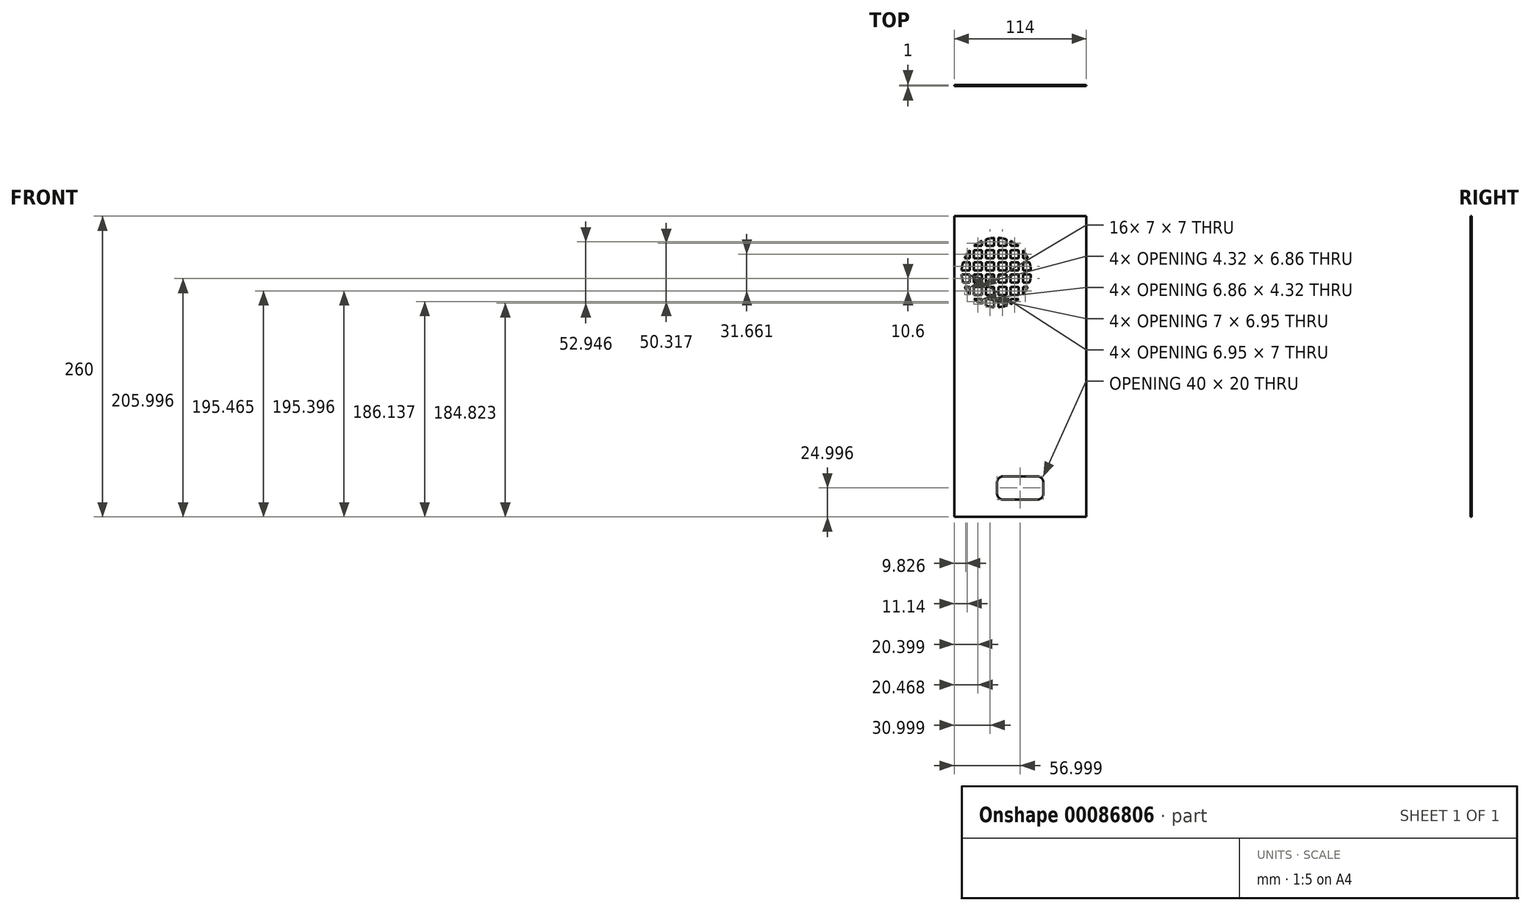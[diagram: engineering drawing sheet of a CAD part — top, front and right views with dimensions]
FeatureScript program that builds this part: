
annotation { "Feature Type Name" : "Feature", "Feature Type Description" : "" }
export const myFeature = defineFeature(function(context is Context, id is Id, definition is map)
    precondition{}
    {
        {
            var Q0;
            Q0=qCreatedBy(makeId("Front.planeOp"),FACE);
            var sketch = newSketch(context, id + "F0", { "sketchPlane" : qUnion([Q0])});
            skLineSegment(sketch, "E0.bottom", {"start": v(-87.72, 200.1) * mm, "end": v(26.28, 200.1) * mm});
            skLineSegment(sketch, "E0.top", {"start": v(-87.72, -59.9) * mm, "end": v(26.28, -59.9) * mm});
            skLineSegment(sketch, "E0.left", {"start": v(-87.72, 200.1) * mm, "end": v(-87.72, -59.9) * mm});
            skLineSegment(sketch, "E0.right", {"start": v(26.28, 200.1) * mm, "end": v(26.28, -59.9) * mm});
            skCircle(sketch, "E1", {"center": v(-51.42, 151.4) * mm, "radius": 30 * mm});
            skLineSegment(sketch, "E2.bottom", {"start": v(-81.42, 181.4) * mm, "end": v(-74.42, 181.4) * mm});
            skLineSegment(sketch, "E2.top", {"start": v(-81.42, 174.4) * mm, "end": v(-74.42, 174.4) * mm});
            skLineSegment(sketch, "E2.left", {"start": v(-81.42, 181.4) * mm, "end": v(-81.42, 174.4) * mm});
            skLineSegment(sketch, "E2.right", {"start": v(-74.42, 181.4) * mm, "end": v(-74.42, 174.4) * mm});
            skLineSegment(sketch, "E3.0.1.0", {"start": v(-81.42, 163.8) * mm, "end": v(-74.42, 163.8) * mm});
            skLineSegment(sketch, "E3.0.1.1", {"start": v(-81.42, 170.8) * mm, "end": v(-81.42, 163.8) * mm});
            skLineSegment(sketch, "E3.0.1.2", {"start": v(-74.42, 170.8) * mm, "end": v(-74.42, 163.8) * mm});
            skLineSegment(sketch, "E3.0.1.3", {"start": v(-81.42, 170.8) * mm, "end": v(-74.42, 170.8) * mm});
            skLineSegment(sketch, "E3.0.2.0", {"start": v(-81.42, 153.2) * mm, "end": v(-74.42, 153.2) * mm});
            skLineSegment(sketch, "E3.0.2.1", {"start": v(-81.42, 160.2) * mm, "end": v(-81.42, 153.2) * mm});
            skLineSegment(sketch, "E3.0.2.2", {"start": v(-74.42, 160.2) * mm, "end": v(-74.42, 153.2) * mm});
            skLineSegment(sketch, "E3.0.2.3", {"start": v(-81.42, 160.2) * mm, "end": v(-74.42, 160.2) * mm});
            skLineSegment(sketch, "E3.0.3.0", {"start": v(-81.42, 142.6) * mm, "end": v(-74.42, 142.6) * mm});
            skLineSegment(sketch, "E3.0.3.1", {"start": v(-81.42, 149.6) * mm, "end": v(-81.42, 142.6) * mm});
            skLineSegment(sketch, "E3.0.3.2", {"start": v(-74.42, 149.6) * mm, "end": v(-74.42, 142.6) * mm});
            skLineSegment(sketch, "E3.0.3.3", {"start": v(-81.42, 149.6) * mm, "end": v(-74.42, 149.6) * mm});
            skLineSegment(sketch, "E3.0.4.0", {"start": v(-81.42, 132) * mm, "end": v(-74.42, 132) * mm});
            skLineSegment(sketch, "E3.0.4.1", {"start": v(-81.42, 139) * mm, "end": v(-81.42, 132) * mm});
            skLineSegment(sketch, "E3.0.4.2", {"start": v(-74.42, 139) * mm, "end": v(-74.42, 132) * mm});
            skLineSegment(sketch, "E3.0.4.3", {"start": v(-81.42, 139) * mm, "end": v(-74.42, 139) * mm});
            skLineSegment(sketch, "E3.0.5.0", {"start": v(-81.42, 121.4) * mm, "end": v(-74.42, 121.4) * mm});
            skLineSegment(sketch, "E3.0.5.1", {"start": v(-81.42, 128.4) * mm, "end": v(-81.42, 121.4) * mm});
            skLineSegment(sketch, "E3.0.5.2", {"start": v(-74.42, 128.4) * mm, "end": v(-74.42, 121.4) * mm});
            skLineSegment(sketch, "E3.0.5.3", {"start": v(-81.42, 128.4) * mm, "end": v(-74.42, 128.4) * mm});
            skLineSegment(sketch, "E3.0.6.0", {"start": v(-81.42, 110.8) * mm, "end": v(-74.42, 110.8) * mm});
            skLineSegment(sketch, "E3.0.6.1", {"start": v(-81.42, 117.8) * mm, "end": v(-81.42, 110.8) * mm});
            skLineSegment(sketch, "E3.0.6.2", {"start": v(-74.42, 117.8) * mm, "end": v(-74.42, 110.8) * mm});
            skLineSegment(sketch, "E3.0.6.3", {"start": v(-81.42, 117.8) * mm, "end": v(-74.42, 117.8) * mm});
            skLineSegment(sketch, "E3.1.0.0", {"start": v(-70.82, 174.4) * mm, "end": v(-63.82, 174.4) * mm});
            skLineSegment(sketch, "E3.1.0.1", {"start": v(-70.82, 181.4) * mm, "end": v(-70.82, 174.4) * mm});
            skLineSegment(sketch, "E3.1.0.2", {"start": v(-63.82, 181.4) * mm, "end": v(-63.82, 174.4) * mm});
            skLineSegment(sketch, "E3.1.0.3", {"start": v(-70.82, 181.4) * mm, "end": v(-63.82, 181.4) * mm});
            skLineSegment(sketch, "E3.1.1.0", {"start": v(-70.82, 163.8) * mm, "end": v(-63.82, 163.8) * mm});
            skLineSegment(sketch, "E3.1.1.1", {"start": v(-70.82, 170.8) * mm, "end": v(-70.82, 163.8) * mm});
            skLineSegment(sketch, "E3.1.1.2", {"start": v(-63.82, 170.8) * mm, "end": v(-63.82, 163.8) * mm});
            skLineSegment(sketch, "E3.1.1.3", {"start": v(-70.82, 170.8) * mm, "end": v(-63.82, 170.8) * mm});
            skLineSegment(sketch, "E3.1.2.0", {"start": v(-70.82, 153.2) * mm, "end": v(-63.82, 153.2) * mm});
            skLineSegment(sketch, "E3.1.2.1", {"start": v(-70.82, 160.2) * mm, "end": v(-70.82, 153.2) * mm});
            skLineSegment(sketch, "E3.1.2.2", {"start": v(-63.82, 160.2) * mm, "end": v(-63.82, 153.2) * mm});
            skLineSegment(sketch, "E3.1.2.3", {"start": v(-70.82, 160.2) * mm, "end": v(-63.82, 160.2) * mm});
            skLineSegment(sketch, "E3.1.3.0", {"start": v(-70.82, 142.6) * mm, "end": v(-63.82, 142.6) * mm});
            skLineSegment(sketch, "E3.1.3.1", {"start": v(-70.82, 149.6) * mm, "end": v(-70.82, 142.6) * mm});
            skLineSegment(sketch, "E3.1.3.2", {"start": v(-63.82, 149.6) * mm, "end": v(-63.82, 142.6) * mm});
            skLineSegment(sketch, "E3.1.3.3", {"start": v(-70.82, 149.6) * mm, "end": v(-63.82, 149.6) * mm});
            skLineSegment(sketch, "E3.1.4.0", {"start": v(-70.82, 132) * mm, "end": v(-63.82, 132) * mm});
            skLineSegment(sketch, "E3.1.4.1", {"start": v(-70.82, 139) * mm, "end": v(-70.82, 132) * mm});
            skLineSegment(sketch, "E3.1.4.2", {"start": v(-63.82, 139) * mm, "end": v(-63.82, 132) * mm});
            skLineSegment(sketch, "E3.1.4.3", {"start": v(-70.82, 139) * mm, "end": v(-63.82, 139) * mm});
            skLineSegment(sketch, "E3.1.5.0", {"start": v(-70.82, 121.4) * mm, "end": v(-63.82, 121.4) * mm});
            skLineSegment(sketch, "E3.1.5.1", {"start": v(-70.82, 128.4) * mm, "end": v(-70.82, 121.4) * mm});
            skLineSegment(sketch, "E3.1.5.2", {"start": v(-63.82, 128.4) * mm, "end": v(-63.82, 121.4) * mm});
            skLineSegment(sketch, "E3.1.5.3", {"start": v(-70.82, 128.4) * mm, "end": v(-63.82, 128.4) * mm});
            skLineSegment(sketch, "E3.1.6.0", {"start": v(-70.82, 110.8) * mm, "end": v(-63.82, 110.8) * mm});
            skLineSegment(sketch, "E3.1.6.1", {"start": v(-70.82, 117.8) * mm, "end": v(-70.82, 110.8) * mm});
            skLineSegment(sketch, "E3.1.6.2", {"start": v(-63.82, 117.8) * mm, "end": v(-63.82, 110.8) * mm});
            skLineSegment(sketch, "E3.1.6.3", {"start": v(-70.82, 117.8) * mm, "end": v(-63.82, 117.8) * mm});
            skLineSegment(sketch, "E3.2.0.0", {"start": v(-60.22, 174.4) * mm, "end": v(-53.22, 174.4) * mm});
            skLineSegment(sketch, "E3.2.0.1", {"start": v(-60.22, 181.4) * mm, "end": v(-60.22, 174.4) * mm});
            skLineSegment(sketch, "E3.2.0.2", {"start": v(-53.22, 181.4) * mm, "end": v(-53.22, 174.4) * mm});
            skLineSegment(sketch, "E3.2.0.3", {"start": v(-60.22, 181.4) * mm, "end": v(-53.22, 181.4) * mm});
            skLineSegment(sketch, "E3.2.1.0", {"start": v(-60.22, 163.8) * mm, "end": v(-53.22, 163.8) * mm});
            skLineSegment(sketch, "E3.2.1.1", {"start": v(-60.22, 170.8) * mm, "end": v(-60.22, 163.8) * mm});
            skLineSegment(sketch, "E3.2.1.2", {"start": v(-53.22, 170.8) * mm, "end": v(-53.22, 163.8) * mm});
            skLineSegment(sketch, "E3.2.1.3", {"start": v(-60.22, 170.8) * mm, "end": v(-53.22, 170.8) * mm});
            skLineSegment(sketch, "E3.2.2.0", {"start": v(-60.22, 153.2) * mm, "end": v(-53.22, 153.2) * mm});
            skLineSegment(sketch, "E3.2.2.1", {"start": v(-60.22, 160.2) * mm, "end": v(-60.22, 153.2) * mm});
            skLineSegment(sketch, "E3.2.2.2", {"start": v(-53.22, 160.2) * mm, "end": v(-53.22, 153.2) * mm});
            skLineSegment(sketch, "E3.2.2.3", {"start": v(-60.22, 160.2) * mm, "end": v(-53.22, 160.2) * mm});
            skLineSegment(sketch, "E3.2.3.0", {"start": v(-60.22, 142.6) * mm, "end": v(-53.22, 142.6) * mm});
            skLineSegment(sketch, "E3.2.3.1", {"start": v(-60.22, 149.6) * mm, "end": v(-60.22, 142.6) * mm});
            skLineSegment(sketch, "E3.2.3.2", {"start": v(-53.22, 149.6) * mm, "end": v(-53.22, 142.6) * mm});
            skLineSegment(sketch, "E3.2.3.3", {"start": v(-60.22, 149.6) * mm, "end": v(-53.22, 149.6) * mm});
            skLineSegment(sketch, "E3.2.4.0", {"start": v(-60.22, 132) * mm, "end": v(-53.22, 132) * mm});
            skLineSegment(sketch, "E3.2.4.1", {"start": v(-60.22, 139) * mm, "end": v(-60.22, 132) * mm});
            skLineSegment(sketch, "E3.2.4.2", {"start": v(-53.22, 139) * mm, "end": v(-53.22, 132) * mm});
            skLineSegment(sketch, "E3.2.4.3", {"start": v(-60.22, 139) * mm, "end": v(-53.22, 139) * mm});
            skLineSegment(sketch, "E3.2.5.0", {"start": v(-60.22, 121.4) * mm, "end": v(-53.22, 121.4) * mm});
            skLineSegment(sketch, "E3.2.5.1", {"start": v(-60.22, 128.4) * mm, "end": v(-60.22, 121.4) * mm});
            skLineSegment(sketch, "E3.2.5.2", {"start": v(-53.22, 128.4) * mm, "end": v(-53.22, 121.4) * mm});
            skLineSegment(sketch, "E3.2.5.3", {"start": v(-60.22, 128.4) * mm, "end": v(-53.22, 128.4) * mm});
            skLineSegment(sketch, "E3.2.6.0", {"start": v(-60.22, 110.8) * mm, "end": v(-53.22, 110.8) * mm});
            skLineSegment(sketch, "E3.2.6.1", {"start": v(-60.22, 117.8) * mm, "end": v(-60.22, 110.8) * mm});
            skLineSegment(sketch, "E3.2.6.2", {"start": v(-53.22, 117.8) * mm, "end": v(-53.22, 110.8) * mm});
            skLineSegment(sketch, "E3.2.6.3", {"start": v(-60.22, 117.8) * mm, "end": v(-53.22, 117.8) * mm});
            skLineSegment(sketch, "E3.3.0.0", {"start": v(-49.62, 174.4) * mm, "end": v(-42.62, 174.4) * mm});
            skLineSegment(sketch, "E3.3.0.1", {"start": v(-49.62, 181.4) * mm, "end": v(-49.62, 174.4) * mm});
            skLineSegment(sketch, "E3.3.0.2", {"start": v(-42.62, 181.4) * mm, "end": v(-42.62, 174.4) * mm});
            skLineSegment(sketch, "E3.3.0.3", {"start": v(-49.62, 181.4) * mm, "end": v(-42.62, 181.4) * mm});
            skLineSegment(sketch, "E3.3.1.0", {"start": v(-49.62, 163.8) * mm, "end": v(-42.62, 163.8) * mm});
            skLineSegment(sketch, "E3.3.1.1", {"start": v(-49.62, 170.8) * mm, "end": v(-49.62, 163.8) * mm});
            skLineSegment(sketch, "E3.3.1.2", {"start": v(-42.62, 170.8) * mm, "end": v(-42.62, 163.8) * mm});
            skLineSegment(sketch, "E3.3.1.3", {"start": v(-49.62, 170.8) * mm, "end": v(-42.62, 170.8) * mm});
            skLineSegment(sketch, "E3.3.2.0", {"start": v(-49.62, 153.2) * mm, "end": v(-42.62, 153.2) * mm});
            skLineSegment(sketch, "E3.3.2.1", {"start": v(-49.62, 160.2) * mm, "end": v(-49.62, 153.2) * mm});
            skLineSegment(sketch, "E3.3.2.2", {"start": v(-42.62, 160.2) * mm, "end": v(-42.62, 153.2) * mm});
            skLineSegment(sketch, "E3.3.2.3", {"start": v(-49.62, 160.2) * mm, "end": v(-42.62, 160.2) * mm});
            skLineSegment(sketch, "E3.3.3.0", {"start": v(-49.62, 142.6) * mm, "end": v(-42.62, 142.6) * mm});
            skLineSegment(sketch, "E3.3.3.1", {"start": v(-49.62, 149.6) * mm, "end": v(-49.62, 142.6) * mm});
            skLineSegment(sketch, "E3.3.3.2", {"start": v(-42.62, 149.6) * mm, "end": v(-42.62, 142.6) * mm});
            skLineSegment(sketch, "E3.3.3.3", {"start": v(-49.62, 149.6) * mm, "end": v(-42.62, 149.6) * mm});
            skLineSegment(sketch, "E3.3.4.0", {"start": v(-49.62, 132) * mm, "end": v(-42.62, 132) * mm});
            skLineSegment(sketch, "E3.3.4.1", {"start": v(-49.62, 139) * mm, "end": v(-49.62, 132) * mm});
            skLineSegment(sketch, "E3.3.4.2", {"start": v(-42.62, 139) * mm, "end": v(-42.62, 132) * mm});
            skLineSegment(sketch, "E3.3.4.3", {"start": v(-49.62, 139) * mm, "end": v(-42.62, 139) * mm});
            skLineSegment(sketch, "E3.3.5.0", {"start": v(-49.62, 121.4) * mm, "end": v(-42.62, 121.4) * mm});
            skLineSegment(sketch, "E3.3.5.1", {"start": v(-49.62, 128.4) * mm, "end": v(-49.62, 121.4) * mm});
            skLineSegment(sketch, "E3.3.5.2", {"start": v(-42.62, 128.4) * mm, "end": v(-42.62, 121.4) * mm});
            skLineSegment(sketch, "E3.3.5.3", {"start": v(-49.62, 128.4) * mm, "end": v(-42.62, 128.4) * mm});
            skLineSegment(sketch, "E3.3.6.0", {"start": v(-49.62, 110.8) * mm, "end": v(-42.62, 110.8) * mm});
            skLineSegment(sketch, "E3.3.6.1", {"start": v(-49.62, 117.8) * mm, "end": v(-49.62, 110.8) * mm});
            skLineSegment(sketch, "E3.3.6.2", {"start": v(-42.62, 117.8) * mm, "end": v(-42.62, 110.8) * mm});
            skLineSegment(sketch, "E3.3.6.3", {"start": v(-49.62, 117.8) * mm, "end": v(-42.62, 117.8) * mm});
            skLineSegment(sketch, "E3.4.0.0", {"start": v(-39.02, 174.4) * mm, "end": v(-32.02, 174.4) * mm});
            skLineSegment(sketch, "E3.4.0.1", {"start": v(-39.02, 181.4) * mm, "end": v(-39.02, 174.4) * mm});
            skLineSegment(sketch, "E3.4.0.2", {"start": v(-32.02, 181.4) * mm, "end": v(-32.02, 174.4) * mm});
            skLineSegment(sketch, "E3.4.0.3", {"start": v(-39.02, 181.4) * mm, "end": v(-32.02, 181.4) * mm});
            skLineSegment(sketch, "E3.4.1.0", {"start": v(-39.02, 163.8) * mm, "end": v(-32.02, 163.8) * mm});
            skLineSegment(sketch, "E3.4.1.1", {"start": v(-39.02, 170.8) * mm, "end": v(-39.02, 163.8) * mm});
            skLineSegment(sketch, "E3.4.1.2", {"start": v(-32.02, 170.8) * mm, "end": v(-32.02, 163.8) * mm});
            skLineSegment(sketch, "E3.4.1.3", {"start": v(-39.02, 170.8) * mm, "end": v(-32.02, 170.8) * mm});
            skLineSegment(sketch, "E3.4.2.0", {"start": v(-39.02, 153.2) * mm, "end": v(-32.02, 153.2) * mm});
            skLineSegment(sketch, "E3.4.2.1", {"start": v(-39.02, 160.2) * mm, "end": v(-39.02, 153.2) * mm});
            skLineSegment(sketch, "E3.4.2.2", {"start": v(-32.02, 160.2) * mm, "end": v(-32.02, 153.2) * mm});
            skLineSegment(sketch, "E3.4.2.3", {"start": v(-39.02, 160.2) * mm, "end": v(-32.02, 160.2) * mm});
            skLineSegment(sketch, "E3.4.3.0", {"start": v(-39.02, 142.6) * mm, "end": v(-32.02, 142.6) * mm});
            skLineSegment(sketch, "E3.4.3.1", {"start": v(-39.02, 149.6) * mm, "end": v(-39.02, 142.6) * mm});
            skLineSegment(sketch, "E3.4.3.2", {"start": v(-32.02, 149.6) * mm, "end": v(-32.02, 142.6) * mm});
            skLineSegment(sketch, "E3.4.3.3", {"start": v(-39.02, 149.6) * mm, "end": v(-32.02, 149.6) * mm});
            skLineSegment(sketch, "E3.4.4.0", {"start": v(-39.02, 132) * mm, "end": v(-32.02, 132) * mm});
            skLineSegment(sketch, "E3.4.4.1", {"start": v(-39.02, 139) * mm, "end": v(-39.02, 132) * mm});
            skLineSegment(sketch, "E3.4.4.2", {"start": v(-32.02, 139) * mm, "end": v(-32.02, 132) * mm});
            skLineSegment(sketch, "E3.4.4.3", {"start": v(-39.02, 139) * mm, "end": v(-32.02, 139) * mm});
            skLineSegment(sketch, "E3.4.5.0", {"start": v(-39.02, 121.4) * mm, "end": v(-32.02, 121.4) * mm});
            skLineSegment(sketch, "E3.4.5.1", {"start": v(-39.02, 128.4) * mm, "end": v(-39.02, 121.4) * mm});
            skLineSegment(sketch, "E3.4.5.2", {"start": v(-32.02, 128.4) * mm, "end": v(-32.02, 121.4) * mm});
            skLineSegment(sketch, "E3.4.5.3", {"start": v(-39.02, 128.4) * mm, "end": v(-32.02, 128.4) * mm});
            skLineSegment(sketch, "E3.4.6.0", {"start": v(-39.02, 110.8) * mm, "end": v(-32.02, 110.8) * mm});
            skLineSegment(sketch, "E3.4.6.1", {"start": v(-39.02, 117.8) * mm, "end": v(-39.02, 110.8) * mm});
            skLineSegment(sketch, "E3.4.6.2", {"start": v(-32.02, 117.8) * mm, "end": v(-32.02, 110.8) * mm});
            skLineSegment(sketch, "E3.4.6.3", {"start": v(-39.02, 117.8) * mm, "end": v(-32.02, 117.8) * mm});
            skLineSegment(sketch, "E3.5.0.0", {"start": v(-28.42, 174.4) * mm, "end": v(-21.42, 174.4) * mm});
            skLineSegment(sketch, "E3.5.0.1", {"start": v(-28.42, 181.4) * mm, "end": v(-28.42, 174.4) * mm});
            skLineSegment(sketch, "E3.5.0.2", {"start": v(-21.42, 181.4) * mm, "end": v(-21.42, 174.4) * mm});
            skLineSegment(sketch, "E3.5.0.3", {"start": v(-28.42, 181.4) * mm, "end": v(-21.42, 181.4) * mm});
            skLineSegment(sketch, "E3.5.1.0", {"start": v(-28.42, 163.8) * mm, "end": v(-21.42, 163.8) * mm});
            skLineSegment(sketch, "E3.5.1.1", {"start": v(-28.42, 170.8) * mm, "end": v(-28.42, 163.8) * mm});
            skLineSegment(sketch, "E3.5.1.2", {"start": v(-21.42, 170.8) * mm, "end": v(-21.42, 163.8) * mm});
            skLineSegment(sketch, "E3.5.1.3", {"start": v(-28.42, 170.8) * mm, "end": v(-21.42, 170.8) * mm});
            skLineSegment(sketch, "E3.5.2.0", {"start": v(-28.42, 153.2) * mm, "end": v(-21.42, 153.2) * mm});
            skLineSegment(sketch, "E3.5.2.1", {"start": v(-28.42, 160.2) * mm, "end": v(-28.42, 153.2) * mm});
            skLineSegment(sketch, "E3.5.2.2", {"start": v(-21.42, 160.2) * mm, "end": v(-21.42, 153.2) * mm});
            skLineSegment(sketch, "E3.5.2.3", {"start": v(-28.42, 160.2) * mm, "end": v(-21.42, 160.2) * mm});
            skLineSegment(sketch, "E3.5.3.0", {"start": v(-28.42, 142.6) * mm, "end": v(-21.42, 142.6) * mm});
            skLineSegment(sketch, "E3.5.3.1", {"start": v(-28.42, 149.6) * mm, "end": v(-28.42, 142.6) * mm});
            skLineSegment(sketch, "E3.5.3.2", {"start": v(-21.42, 149.6) * mm, "end": v(-21.42, 142.6) * mm});
            skLineSegment(sketch, "E3.5.3.3", {"start": v(-28.42, 149.6) * mm, "end": v(-21.42, 149.6) * mm});
            skLineSegment(sketch, "E3.5.4.0", {"start": v(-28.42, 132) * mm, "end": v(-21.42, 132) * mm});
            skLineSegment(sketch, "E3.5.4.1", {"start": v(-28.42, 139) * mm, "end": v(-28.42, 132) * mm});
            skLineSegment(sketch, "E3.5.4.2", {"start": v(-21.42, 139) * mm, "end": v(-21.42, 132) * mm});
            skLineSegment(sketch, "E3.5.4.3", {"start": v(-28.42, 139) * mm, "end": v(-21.42, 139) * mm});
            skLineSegment(sketch, "E3.5.5.0", {"start": v(-28.42, 121.4) * mm, "end": v(-21.42, 121.4) * mm});
            skLineSegment(sketch, "E3.5.5.1", {"start": v(-28.42, 128.4) * mm, "end": v(-28.42, 121.4) * mm});
            skLineSegment(sketch, "E3.5.5.2", {"start": v(-21.42, 128.4) * mm, "end": v(-21.42, 121.4) * mm});
            skLineSegment(sketch, "E3.5.5.3", {"start": v(-28.42, 128.4) * mm, "end": v(-21.42, 128.4) * mm});
            skLineSegment(sketch, "E3.5.6.0", {"start": v(-28.42, 110.8) * mm, "end": v(-21.42, 110.8) * mm});
            skLineSegment(sketch, "E3.5.6.1", {"start": v(-28.42, 117.8) * mm, "end": v(-28.42, 110.8) * mm});
            skLineSegment(sketch, "E3.5.6.2", {"start": v(-21.42, 117.8) * mm, "end": v(-21.42, 110.8) * mm});
            skLineSegment(sketch, "E3.5.6.3", {"start": v(-28.42, 117.8) * mm, "end": v(-21.42, 117.8) * mm});
            skLineSegment(sketch, "E3.6.0.0", {"start": v(-17.82, 174.4) * mm, "end": v(-10.82, 174.4) * mm});
            skLineSegment(sketch, "E3.6.0.1", {"start": v(-17.82, 181.4) * mm, "end": v(-17.82, 174.4) * mm});
            skLineSegment(sketch, "E3.6.0.2", {"start": v(-10.82, 181.4) * mm, "end": v(-10.82, 174.4) * mm});
            skLineSegment(sketch, "E3.6.0.3", {"start": v(-17.82, 181.4) * mm, "end": v(-10.82, 181.4) * mm});
            skLineSegment(sketch, "E3.6.1.0", {"start": v(-17.82, 163.8) * mm, "end": v(-10.82, 163.8) * mm});
            skLineSegment(sketch, "E3.6.1.1", {"start": v(-17.82, 170.8) * mm, "end": v(-17.82, 163.8) * mm});
            skLineSegment(sketch, "E3.6.1.2", {"start": v(-10.82, 170.8) * mm, "end": v(-10.82, 163.8) * mm});
            skLineSegment(sketch, "E3.6.1.3", {"start": v(-17.82, 170.8) * mm, "end": v(-10.82, 170.8) * mm});
            skLineSegment(sketch, "E3.6.2.0", {"start": v(-17.82, 153.2) * mm, "end": v(-10.82, 153.2) * mm});
            skLineSegment(sketch, "E3.6.2.1", {"start": v(-17.82, 160.2) * mm, "end": v(-17.82, 153.2) * mm});
            skLineSegment(sketch, "E3.6.2.2", {"start": v(-10.82, 160.2) * mm, "end": v(-10.82, 153.2) * mm});
            skLineSegment(sketch, "E3.6.2.3", {"start": v(-17.82, 160.2) * mm, "end": v(-10.82, 160.2) * mm});
            skLineSegment(sketch, "E3.6.3.0", {"start": v(-17.82, 142.6) * mm, "end": v(-10.82, 142.6) * mm});
            skLineSegment(sketch, "E3.6.3.1", {"start": v(-17.82, 149.6) * mm, "end": v(-17.82, 142.6) * mm});
            skLineSegment(sketch, "E3.6.3.2", {"start": v(-10.82, 149.6) * mm, "end": v(-10.82, 142.6) * mm});
            skLineSegment(sketch, "E3.6.3.3", {"start": v(-17.82, 149.6) * mm, "end": v(-10.82, 149.6) * mm});
            skLineSegment(sketch, "E3.6.4.0", {"start": v(-17.82, 132) * mm, "end": v(-10.82, 132) * mm});
            skLineSegment(sketch, "E3.6.4.1", {"start": v(-17.82, 139) * mm, "end": v(-17.82, 132) * mm});
            skLineSegment(sketch, "E3.6.4.2", {"start": v(-10.82, 139) * mm, "end": v(-10.82, 132) * mm});
            skLineSegment(sketch, "E3.6.4.3", {"start": v(-17.82, 139) * mm, "end": v(-10.82, 139) * mm});
            skLineSegment(sketch, "E3.6.5.0", {"start": v(-17.82, 121.4) * mm, "end": v(-10.82, 121.4) * mm});
            skLineSegment(sketch, "E3.6.5.1", {"start": v(-17.82, 128.4) * mm, "end": v(-17.82, 121.4) * mm});
            skLineSegment(sketch, "E3.6.5.2", {"start": v(-10.82, 128.4) * mm, "end": v(-10.82, 121.4) * mm});
            skLineSegment(sketch, "E3.6.5.3", {"start": v(-17.82, 128.4) * mm, "end": v(-10.82, 128.4) * mm});
            skLineSegment(sketch, "E3.6.6.0", {"start": v(-17.82, 110.8) * mm, "end": v(-10.82, 110.8) * mm});
            skLineSegment(sketch, "E3.6.6.1", {"start": v(-17.82, 117.8) * mm, "end": v(-17.82, 110.8) * mm});
            skLineSegment(sketch, "E3.6.6.2", {"start": v(-10.82, 117.8) * mm, "end": v(-10.82, 110.8) * mm});
            skLineSegment(sketch, "E3.6.6.3", {"start": v(-17.82, 117.8) * mm, "end": v(-10.82, 117.8) * mm});
            skLineSegment(sketch, "E3.direction1", {"start": v(-81.42, 174.4) * mm, "end": v(-70.82, 174.4) * mm, "construction": true});
            skLineSegment(sketch, "E3.direction2", {"start": v(-81.42, 174.4) * mm, "end": v(-81.42, 163.8) * mm, "construction": true});
            skLineSegment(sketch, "E4", {"start": v(-30.72, 200.1) * mm, "end": v(-30.72, -81.7) * mm, "construction": true});
            skLineSegment(sketch, "E5.bottom", {"start": v(-45.72, -24.9) * mm, "end": v(-15.72, -24.9) * mm});
            skLineSegment(sketch, "E5.top", {"start": v(-45.72, -44.9) * mm, "end": v(-15.72, -44.9) * mm});
            skLineSegment(sketch, "E5.left", {"start": v(-50.72, -29.9) * mm, "end": v(-50.72, -39.9) * mm});
            skLineSegment(sketch, "E5.right", {"start": v(-10.72, -29.9) * mm, "end": v(-10.72, -39.9) * mm});
            skPoint(sketch, "E5.middle", {"position": v(-30.72, -34.9) * mm});
            skPoint(sketch, "E6.visualSharp", {"position": v(-50.72, -24.9) * mm});
            skArc(sketch, "E6.filletArc", {"start": v(-45.72, -24.9) * mm, "mid": v(-49.26, -26.37) * mm, "end": v(-50.72, -29.9) * mm});
            skPoint(sketch, "E7.visualSharp", {"position": v(-50.72, -44.9) * mm});
            skArc(sketch, "E7.filletArc", {"start": v(-50.72, -39.9) * mm, "mid": v(-49.26, -43.44) * mm, "end": v(-45.72, -44.9) * mm});
            skPoint(sketch, "E8.visualSharp", {"position": v(-10.72, -44.9) * mm});
            skArc(sketch, "E8.filletArc", {"start": v(-15.72, -44.9) * mm, "mid": v(-12.19, -43.44) * mm, "end": v(-10.72, -39.9) * mm});
            skPoint(sketch, "E9.visualSharp", {"position": v(-10.72, -24.9) * mm});
            skArc(sketch, "E9.filletArc", {"start": v(-10.72, -29.9) * mm, "mid": v(-12.19, -26.37) * mm, "end": v(-15.72, -24.9) * mm});
            skSolve(sketch);
        }
        {
            var Q0;
            Q0 = qSketchRegion(id + "F0", true);
            var Q1;
            {var subQ32=sQuery(id+"F0.wireOp",EDGE,"E3.0.2.2");Q1=makeQuery(id+"F0.imprint","IMPRINT",FACE,{"disambiguationData":[TD([[makeQuery(id+"F0.imprint","IMPRINT",EDGE,{"derivedFrom":subQ32}),1.0]])]});}
            var Q2;
            Q2=makeQuery(id+"F0.imprint","IMPRINT",FACE,{"disambiguationData":[TD([[makeQuery(id+"F0.imprint","IMPRINT",EDGE,{"derivedFrom":sQuery(id+"F0.wireOp",EDGE,"E2.bottom")}),-1.0]])]});
            var Q3;
            {var subQ4=sQuery(id+"F0.wireOp",EDGE,"E3.1.0.1");Q3=makeQuery(id+"F0.imprint","IMPRINT",FACE,{"disambiguationData":[TD([[makeQuery(id+"F0.imprint","IMPRINT",EDGE,{"derivedFrom":subQ4}),1.0]])]});}
            var Q4;
            {var subQ6=sQuery(id+"F0.wireOp",EDGE,"E3.0.1.1");Q4=makeQuery(id+"F0.imprint","IMPRINT",FACE,{"disambiguationData":[TD([[makeQuery(id+"F0.imprint","IMPRINT",EDGE,{"derivedFrom":subQ6}),1.0]])]});}
            var Q5;
            {var subQ1=sQuery(id+"F0.wireOp",EDGE,"E3.0.4.0");Q5=makeQuery(id+"F0.imprint","IMPRINT",FACE,{"disambiguationData":[TD([[makeQuery(id+"F0.imprint","IMPRINT",EDGE,{"derivedFrom":subQ1}),1.0]])]});}
            var Q6;
            Q6=makeQuery(id+"F0.imprint","IMPRINT",FACE,{"disambiguationData":[TD([[makeQuery(id+"F0.imprint","IMPRINT",EDGE,{"derivedFrom":sQuery(id+"F0.wireOp",EDGE,"E3.0.5.0")}),1.0]])]});
            var Q7;
            Q7=makeQuery(id+"F0.imprint","IMPRINT",FACE,{"disambiguationData":[TD([[makeQuery(id+"F0.imprint","IMPRINT",EDGE,{"derivedFrom":sQuery(id+"F0.wireOp",EDGE,"E3.0.6.0")}),1.0]])]});
            var Q8;
            {var subQ1=sQuery(id+"F0.wireOp",EDGE,"E3.1.5.0");Q8=makeQuery(id+"F0.imprint","IMPRINT",FACE,{"disambiguationData":[TD([[makeQuery(id+"F0.imprint","IMPRINT",EDGE,{"derivedFrom":subQ1}),1.0]])]});}
            var Q9;
            Q9=makeQuery(id+"F0.imprint","IMPRINT",FACE,{"disambiguationData":[TD([[makeQuery(id+"F0.imprint","IMPRINT",EDGE,{"derivedFrom":sQuery(id+"F0.wireOp",EDGE,"E3.1.6.0")}),1.0]])]});
            var Q10;
            Q10=makeQuery(id+"F0.imprint","IMPRINT",FACE,{"disambiguationData":[TD([[makeQuery(id+"F0.imprint","IMPRINT",EDGE,{"derivedFrom":sQuery(id+"F0.wireOp",EDGE,"E3.2.6.0")}),1.0]])]});
            var Q11;
            Q11=makeQuery(id+"F0.imprint","IMPRINT",FACE,{"disambiguationData":[TD([[makeQuery(id+"F0.imprint","IMPRINT",EDGE,{"derivedFrom":sQuery(id+"F0.wireOp",EDGE,"E3.3.6.0")}),1.0]])]});
            var Q12;
            Q12=makeQuery(id+"F0.imprint","IMPRINT",FACE,{"disambiguationData":[TD([[makeQuery(id+"F0.imprint","IMPRINT",EDGE,{"derivedFrom":sQuery(id+"F0.wireOp",EDGE,"E3.4.6.0")}),1.0]])]});
            var Q13;
            {var subQ2=sQuery(id+"F0.wireOp",EDGE,"E3.4.5.0");Q13=makeQuery(id+"F0.imprint","IMPRINT",FACE,{"disambiguationData":[TD([[makeQuery(id+"F0.imprint","IMPRINT",EDGE,{"derivedFrom":subQ2}),1.0]])]});}
            var Q14;
            Q14=makeQuery(id+"F0.imprint","IMPRINT",FACE,{"disambiguationData":[TD([[makeQuery(id+"F0.imprint","IMPRINT",EDGE,{"derivedFrom":sQuery(id+"F0.wireOp",EDGE,"E3.5.5.0")}),1.0]])]});
            var Q15;
            Q15=makeQuery(id+"F0.imprint","IMPRINT",FACE,{"disambiguationData":[TD([[makeQuery(id+"F0.imprint","IMPRINT",EDGE,{"derivedFrom":sQuery(id+"F0.wireOp",EDGE,"E3.5.6.0")}),1.0]])]});
            var Q16;
            Q16=makeQuery(id+"F0.imprint","IMPRINT",FACE,{"disambiguationData":[TD([[makeQuery(id+"F0.imprint","IMPRINT",EDGE,{"derivedFrom":sQuery(id+"F0.wireOp",EDGE,"E3.6.6.0")}),1.0]])]});
            var Q17;
            Q17=makeQuery(id+"F0.imprint","IMPRINT",FACE,{"disambiguationData":[TD([[makeQuery(id+"F0.imprint","IMPRINT",EDGE,{"derivedFrom":sQuery(id+"F0.wireOp",EDGE,"E3.6.5.0")}),1.0]])]});
            var Q18;
            Q18=makeQuery(id+"F0.imprint","IMPRINT",FACE,{"disambiguationData":[TD([[makeQuery(id+"F0.imprint","IMPRINT",EDGE,{"derivedFrom":sQuery(id+"F0.wireOp",EDGE,"E3.6.4.0")}),1.0]])]});
            var Q19;
            {var subQ2=sQuery(id+"F0.wireOp",EDGE,"E3.5.4.0");Q19=makeQuery(id+"F0.imprint","IMPRINT",FACE,{"disambiguationData":[TD([[makeQuery(id+"F0.imprint","IMPRINT",EDGE,{"derivedFrom":subQ2}),1.0]])]});}
            var Q20;
            Q20=makeQuery(id+"F0.imprint","IMPRINT",FACE,{"disambiguationData":[TD([[makeQuery(id+"F0.imprint","IMPRINT",EDGE,{"derivedFrom":sQuery(id+"F0.wireOp",EDGE,"E3.6.3.0")}),1.0]])]});
            var Q21;
            Q21=makeQuery(id+"F0.imprint","IMPRINT",FACE,{"disambiguationData":[TD([[makeQuery(id+"F0.imprint","IMPRINT",EDGE,{"derivedFrom":sQuery(id+"F0.wireOp",EDGE,"E3.6.2.0")}),1.0]])]});
            var Q22;
            Q22=makeQuery(id+"F0.imprint","IMPRINT",FACE,{"disambiguationData":[TD([[makeQuery(id+"F0.imprint","IMPRINT",EDGE,{"derivedFrom":sQuery(id+"F0.wireOp",EDGE,"E3.6.1.0")}),1.0]])]});
            var Q23;
            {var subQ4=sQuery(id+"F0.wireOp",EDGE,"E3.5.1.2");Q23=makeQuery(id+"F0.imprint","IMPRINT",FACE,{"disambiguationData":[TD([[makeQuery(id+"F0.imprint","IMPRINT",EDGE,{"derivedFrom":subQ4}),-1.0]])]});}
            var Q24;
            Q24=makeQuery(id+"F0.imprint","IMPRINT",FACE,{"disambiguationData":[TD([[makeQuery(id+"F0.imprint","IMPRINT",EDGE,{"derivedFrom":sQuery(id+"F0.wireOp",EDGE,"E3.6.0.0")}),1.0]])]});
            var Q25;
            Q25=makeQuery(id+"F0.imprint","IMPRINT",FACE,{"disambiguationData":[TD([[makeQuery(id+"F0.imprint","IMPRINT",EDGE,{"derivedFrom":sQuery(id+"F0.wireOp",EDGE,"E3.5.0.0")}),1.0]])]});
            var Q26;
            {var subQ0=sQuery(id+"F0.wireOp",EDGE,"E3.4.0.2");Q26=makeQuery(id+"F0.imprint","IMPRINT",FACE,{"disambiguationData":[TD([[makeQuery(id+"F0.imprint","IMPRINT",EDGE,{"derivedFrom":subQ0}),-1.0]])]});}
            var Q27;
            {var subQ5=sQuery(id+"F0.wireOp",EDGE,"E3.2.0.3");Q27=makeQuery(id+"F0.imprint","IMPRINT",FACE,{"disambiguationData":[TD([[makeQuery(id+"F0.imprint","IMPRINT",EDGE,{"derivedFrom":subQ5}),-1.0]])]});}
            var Q28;
            {var subQ5=sQuery(id+"F0.wireOp",EDGE,"E3.3.0.3");Q28=makeQuery(id+"F0.imprint","IMPRINT",FACE,{"disambiguationData":[TD([[makeQuery(id+"F0.imprint","IMPRINT",EDGE,{"derivedFrom":subQ5}),-1.0]])]});}
            var Q29;
            {var subQ5=sQuery(id+"F0.wireOp",EDGE,"E3.5.2.2");Q29=makeQuery(id+"F0.imprint","IMPRINT",FACE,{"disambiguationData":[TD([[makeQuery(id+"F0.imprint","IMPRINT",EDGE,{"derivedFrom":subQ5}),-1.0]])]});}
            var Q30;
            {var subQ5=sQuery(id+"F0.wireOp",EDGE,"E3.5.3.2");Q30=makeQuery(id+"F0.imprint","IMPRINT",FACE,{"disambiguationData":[TD([[makeQuery(id+"F0.imprint","IMPRINT",EDGE,{"derivedFrom":subQ5}),-1.0]])]});}
            var Q31;
            {var subQ5=sQuery(id+"F0.wireOp",EDGE,"E3.0.2.1");Q31=makeQuery(id+"F0.imprint","IMPRINT",FACE,{"disambiguationData":[TD([[makeQuery(id+"F0.imprint","IMPRINT",EDGE,{"derivedFrom":subQ5}),1.0]])]});}
            var Q32;
            {var subQ5=sQuery(id+"F0.wireOp",EDGE,"E3.0.3.1");Q32=makeQuery(id+"F0.imprint","IMPRINT",FACE,{"disambiguationData":[TD([[makeQuery(id+"F0.imprint","IMPRINT",EDGE,{"derivedFrom":subQ5}),1.0]])]});}
            var Q33;
            {var subQ5=sQuery(id+"F0.wireOp",EDGE,"E3.2.5.0");Q33=makeQuery(id+"F0.imprint","IMPRINT",FACE,{"disambiguationData":[TD([[makeQuery(id+"F0.imprint","IMPRINT",EDGE,{"derivedFrom":subQ5}),1.0]])]});}
            var Q34;
            {var subQ5=sQuery(id+"F0.wireOp",EDGE,"E3.3.5.0");Q34=makeQuery(id+"F0.imprint","IMPRINT",FACE,{"disambiguationData":[TD([[makeQuery(id+"F0.imprint","IMPRINT",EDGE,{"derivedFrom":subQ5}),1.0]])]});}
            extrude(context, id + "F1", {"entities" : qUnion([Q0, Q1, Q2, Q3, Q4, Q5, Q6, Q7, Q8, Q9, Q10, Q11, Q12, Q13, Q14, Q15, Q16, Q17, Q18, Q19, Q20, Q21, Q22, Q23, Q24, Q25, Q26, Q27, Q28, Q29, Q30, Q31, Q32, Q33, Q34]), "depth" : 1 * mm});
        }
    });
